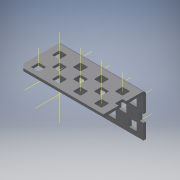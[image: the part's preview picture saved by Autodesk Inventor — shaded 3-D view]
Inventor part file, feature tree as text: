
AUTODESK INVENTOR PART (.ipt)
format: ipt  version: 2017 SP1 (Build 210196100, 196)  size: 1,833,472 bytes
history: native  units: in
note: dims shown in document units (in); Inventor stores cm internally (conversion verified against a paired STEP export)
features: other x29, pattern_linear x4, sheet_metal_op x1, extrude x1, imported_body x1, sketch x1
ambient origin geometry x8: Origin, YZ Plane, XZ Plane, XY Plane, X Axis, Y Axis, Z Axis, Center Point
bodies: Body1 (feature_tree)
feature tree (37):
  sheet_metal_op  "Fold1"
  other  "L-Channel"
  extrude  "length cut"  Depth=0.5in
  other  "top out axis"
  other  "top inner axis"
  other  "back out axis"
  other  "back inner axis"
  pattern_linear  "top outer axes"  Count1=2 Spacing1=0.5in
  pattern_linear  "top inner axes"  Spacing1=0.5in  [1 undecoded]
  pattern_linear  "back outer axes"  Count1=2 Spacing1=0.5in
  pattern_linear  "back inner axes"  Spacing1=0.5in  [1 undecoded]
  other  "right plane"
  imported_body  "Base1"
  sketch  "Sketch1"  dims[d1=0.0in d4=0.5in d5=0.7874in d7=0.5in d10=0.5in d13=0.5in d14=0.7874in d16=0.5in d19=0.5in d20=-2.0in d21=0.0in d22=0.0in d23=0.0in d24=0.0in d25=0.0in d26=0.0in]
  other  "Work Point1"
  other  "Work Point2"
  other  "Work Point3"
  other  "Work Point4"
  other  "Work Axis5"
  other  "Work Axis6"
  other  "Work Axis7"
  other  "Work Axis11"
  other  "Work Axis12"
  other  "Work Axis13"
  other  "Work Axis14"
  other  "Work Axis18"
  other  "Work Axis19"
  other  "Work Axis23"
  other  "Work Axis24"
  other  "Work Axis25"
  other  "Work Axis29"
  other  "Work Axis30"
  other  "Work Axis31"
  other  "Work Axis32"
  other  "Work Axis36"
  other  "Work Axis37"
  other  "left plane"
note: 2 required parameter values undecoded (feature->parameter linkage not recoverable at this tier; creation-order binding heuristic only, values carry confidence <= 0.55)
